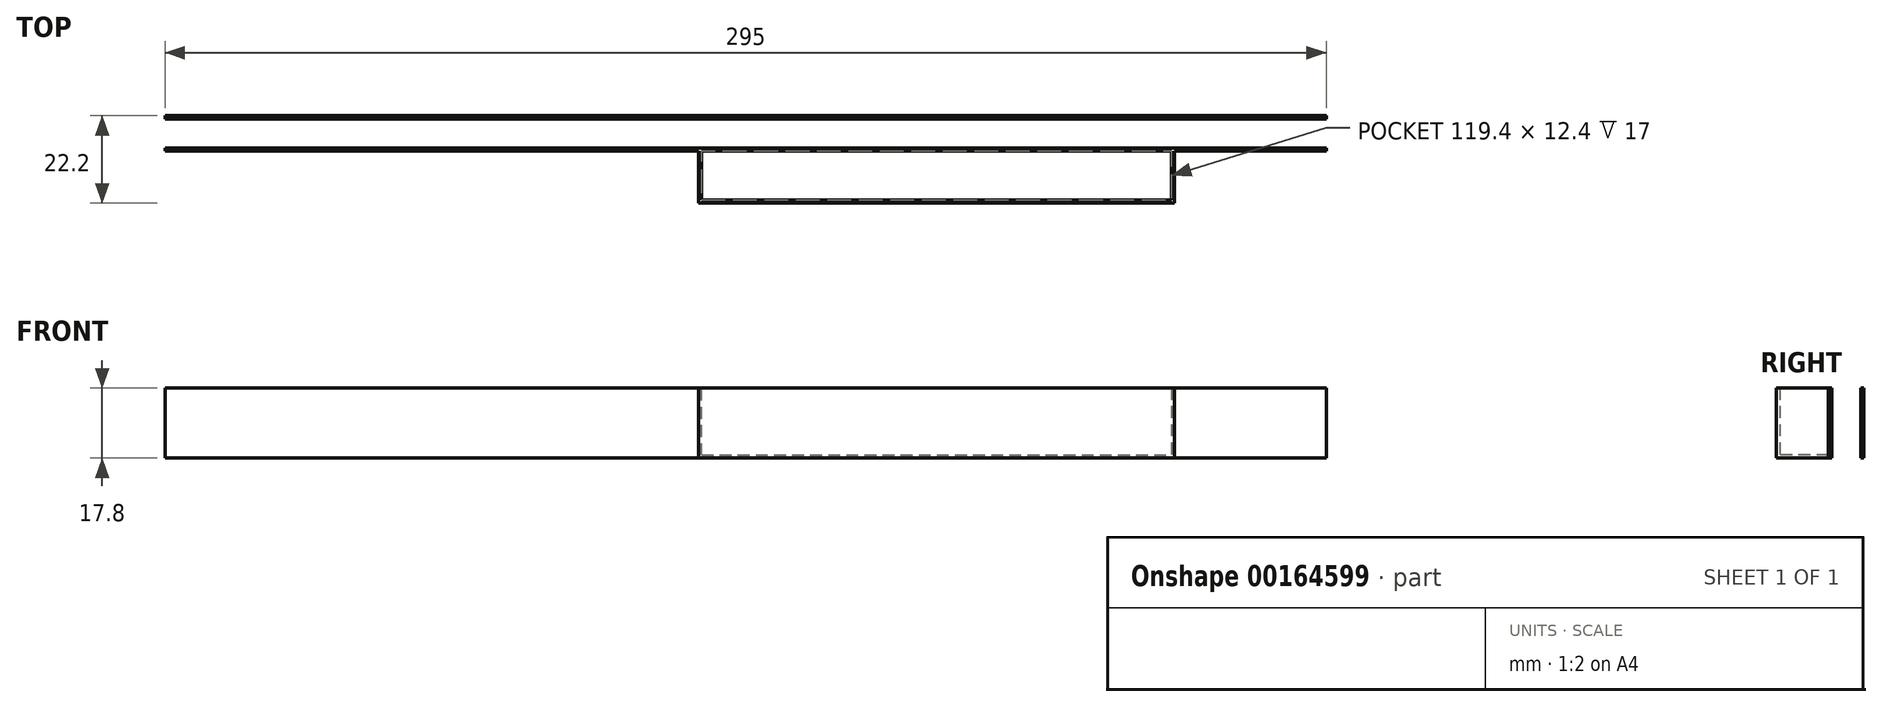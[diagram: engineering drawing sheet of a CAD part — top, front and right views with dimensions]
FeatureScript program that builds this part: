
annotation { "Feature Type Name" : "Feature", "Feature Type Description" : "" }
export const myFeature = defineFeature(function(context is Context, id is Id, definition is map)
    precondition{}
    {
        {
            assignVariable(context, id + "F0", {"name" : "Height", "anyValue" : 17});
        }
        {
            assignVariable(context, id + "F1", {"name" : "Thickness", "anyValue" : 0.8});
        }
        {
            var Q0;
            Q0=qCreatedBy(makeId("Top.planeOp"),FACE);
            var sketch = newSketch(context, id + "F2", { "sketchPlane" : qUnion([Q0])});
            skLineSegment(sketch, "E0.bottom", {"start": v(0, 0) * mm, "end": v(121, 0) * mm});
            skLineSegment(sketch, "E0.top", {"start": v(0, -13.2) * mm, "end": v(121, -13.2) * mm});
            skLineSegment(sketch, "E0.left", {"start": v(0, 0) * mm, "end": v(0, -13.2) * mm});
            skLineSegment(sketch, "E0.right", {"start": v(121, 0) * mm, "end": v(121, -13.2) * mm});
            skLineSegment(sketch, "E1.bottom", {"start": v(-135.5, 0) * mm, "end": v(159.5, 0) * mm});
            skLineSegment(sketch, "E1.top", {"start": v(-135.5, 0.8) * mm, "end": v(159.5, 0.8) * mm});
            skLineSegment(sketch, "E1.left", {"start": v(-135.5, 0) * mm, "end": v(-135.5, 0.8) * mm});
            skLineSegment(sketch, "E1.right", {"start": v(159.5, 0) * mm, "end": v(159.5, 0.8) * mm});
            skLineSegment(sketch, "E2.bottom", {"start": v(-135.5, 0.8) * mm, "end": v(-134.7, 0.8) * mm});
            skLineSegment(sketch, "E2.top", {"start": v(-135.5, 8.2) * mm, "end": v(-134.7, 8.2) * mm});
            skLineSegment(sketch, "E2.left", {"start": v(-135.5, 0.8) * mm, "end": v(-135.5, 8.2) * mm});
            skLineSegment(sketch, "E2.right", {"start": v(-134.7, 0.8) * mm, "end": v(-134.7, 8.2) * mm});
            skLineSegment(sketch, "E3.bottom", {"start": v(-135.5, 8.2) * mm, "end": v(159.5, 8.2) * mm});
            skLineSegment(sketch, "E3.top", {"start": v(-135.5, 9) * mm, "end": v(159.5, 9) * mm});
            skLineSegment(sketch, "E3.left", {"start": v(-135.5, 8.2) * mm, "end": v(-135.5, 9) * mm});
            skLineSegment(sketch, "E3.right", {"start": v(159.5, 8.2) * mm, "end": v(159.5, 9) * mm});
            skLineSegment(sketch, "E4.bottom", {"start": v(159.5, 0.8) * mm, "end": v(158.7, 0.8) * mm});
            skLineSegment(sketch, "E4.top", {"start": v(159.5, 8.2) * mm, "end": v(158.7, 8.2) * mm});
            skLineSegment(sketch, "E4.left", {"start": v(159.5, 0.8) * mm, "end": v(159.5, 8.2) * mm});
            skLineSegment(sketch, "E4.right", {"start": v(158.7, 0.8) * mm, "end": v(158.7, 8.2) * mm});
            skSolve(sketch);
        }
        {
            var Q0;
            Q0=makeQuery(id+"F2.imprint","IMPRINT",FACE,{"disambiguationData":[TD([[makeQuery(id+"F2.imprint","IMPRINT",EDGE,{"derivedFrom":sQuery(id+"F2.wireOp",EDGE,"E3.top")}),-1.0]])]});
            var Q1;
            Q1=makeQuery(id+"F2.imprint","IMPRINT",FACE,{"disambiguationData":[TD([[makeQuery(id+"F2.imprint","IMPRINT",EDGE,{"derivedFrom":sQuery(id+"F2.wireOp",EDGE,"E4.bottom")}),-1.0]])]});
            var Q2;
            Q2=makeQuery(id+"F2.imprint","IMPRINT",FACE,{"disambiguationData":[TD([[makeQuery(id+"F2.imprint","IMPRINT",EDGE,{"derivedFrom":sQuery(id+"F2.wireOp",EDGE,"E2.bottom")}),1.0]])]});
            var Q3;
            Q3=makeQuery(id+"F2.imprint","IMPRINT",FACE,{"disambiguationData":[TD([[makeQuery(id+"F2.imprint","IMPRINT",EDGE,{"derivedFrom":sQuery(id+"F2.wireOp",EDGE,"E0.top")}),1.0]])]});
            var Q4;
            Q4=makeQuery(id+"F2.imprint","IMPRINT",FACE,{"disambiguationData":[TD([[makeQuery(id+"F2.imprint","IMPRINT",EDGE,{"derivedFrom":sQuery(id+"F2.wireOp",EDGE,"E1.top")}),-1.0]])]});
            extrude(context, id + "F3", {"entities" : qUnion([Q0, Q1, Q2, Q3, Q4]), "depth" : (getVariable(context, 'Height') + getVariable(context, 'Thickness')) * mm});
        }
        {
            var Q0;
            Q0=makeQuery(id+"F3.opExtrude","CAP_FACE",FACE,{"disambiguationData":[OSD([sQuery(id+"F2.wireOp",EDGE,"E0.top"),sQuery(id+"F2.wireOp",EDGE,"E0.left"),sQuery(id+"F2.wireOp",EDGE,"E0.right"),sQuery(id+"F2.wireOp",EDGE,"E1.bottom"),sQuery(id+"F2.wireOp",EDGE,"E1.top"),sQuery(id+"F2.wireOp",EDGE,"E1.left"),sQuery(id+"F2.wireOp",EDGE,"E1.right"),sQuery(id+"F2.wireOp",EDGE,"E2.left"),sQuery(id+"F2.wireOp",EDGE,"E2.right"),sQuery(id+"F2.wireOp",EDGE,"E3.bottom"),sQuery(id+"F2.wireOp",EDGE,"E3.top"),sQuery(id+"F2.wireOp",EDGE,"E3.left"),sQuery(id+"F2.wireOp",EDGE,"E3.right"),sQuery(id+"F2.wireOp",EDGE,"E4.left"),sQuery(id+"F2.wireOp",EDGE,"E4.right")])],"isStart":false});
            shell(context, id + "F4", {"entities" : qUnion([Q0]), "thickness" : getVariable(context, 'Thickness') * mm});
        }
    });
